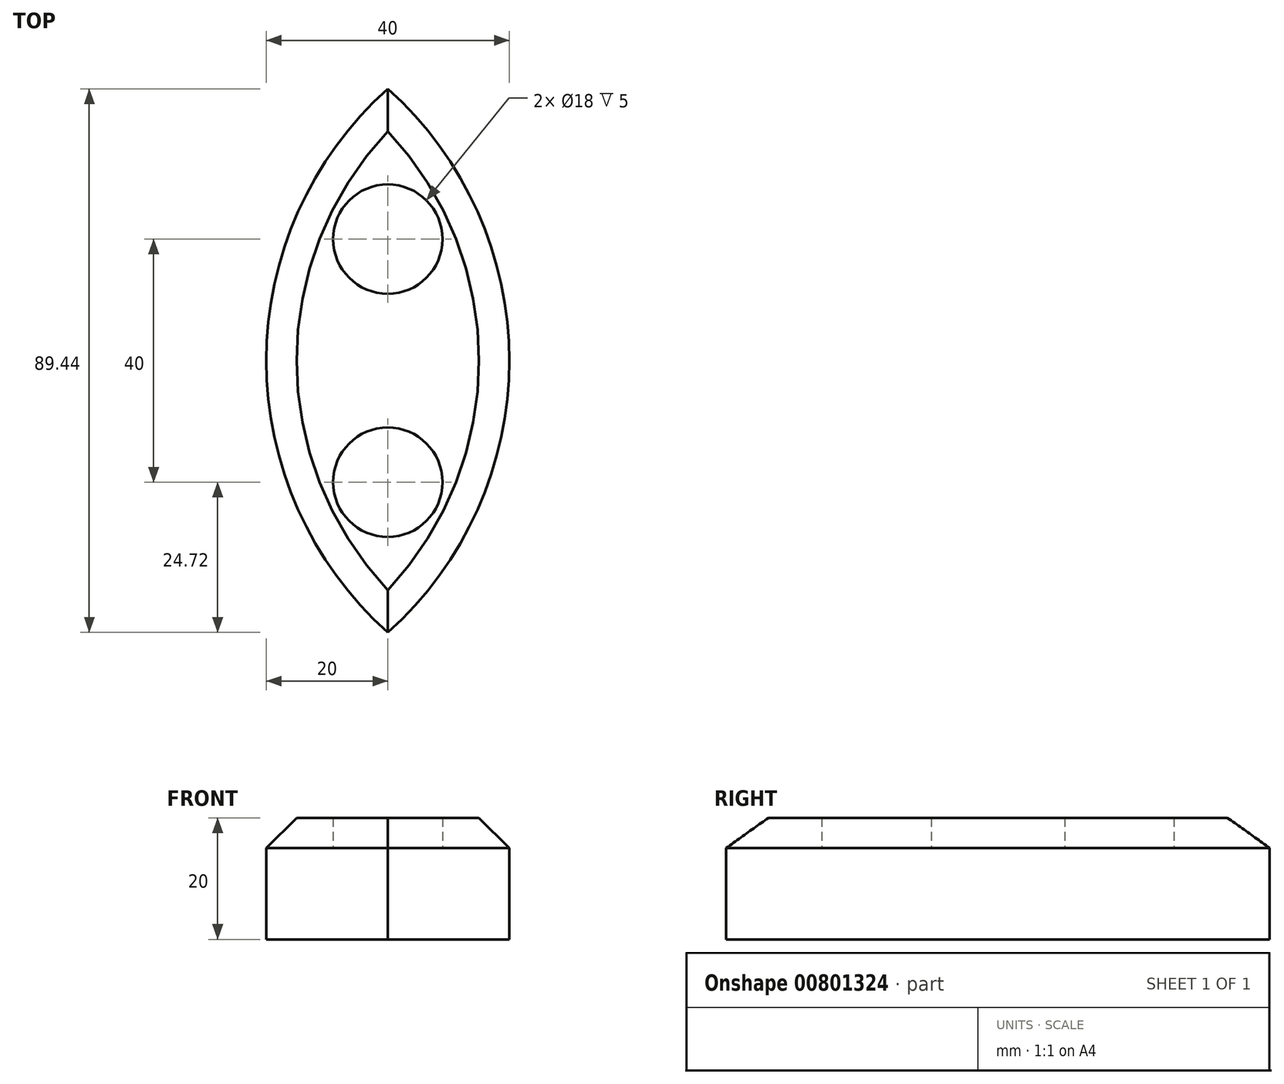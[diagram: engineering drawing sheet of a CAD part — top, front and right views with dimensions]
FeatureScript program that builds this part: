
annotation { "Feature Type Name" : "Feature", "Feature Type Description" : "" }
export const myFeature = defineFeature(function(context is Context, id is Id, definition is map)
    precondition{}
    {
        {
            var Q0;
            Q0=qCreatedBy(makeId("Top.planeOp"),FACE);
            var sketch = newSketch(context, id + "F0", { "sketchPlane" : qUnion([Q0])});
            skLineSegment(sketch, "E0", {"start": v(0, 0) * mm, "end": v(40, 0) * mm});
            skLineSegment(sketch, "E1", {"start": v(0, 0) * mm, "end": v(-40, 0) * mm});
            skPoint(sketch, "E2", {"position": v(-20, 0) * mm});
            skPoint(sketch, "E3", {"position": v(20, 0) * mm});
            skArc(sketch, "E4", {"start": v(0, -44.72) * mm, "mid": v(20, 0) * mm, "end": v(0, 44.72) * mm});
            skArc(sketch, "E5", {"start": v(0, 44.72) * mm, "mid": v(-20, 0) * mm, "end": v(0, -44.72) * mm});
            skPoint(sketch, "E6", {"position": v(0, 20) * mm});
            skPoint(sketch, "E7", {"position": v(0, -20) * mm});
            skCircle(sketch, "E8", {"center": v(0, 20) * mm, "radius": 9 * mm});
            skCircle(sketch, "E9", {"center": v(0, -20) * mm, "radius": 9 * mm});
            skSolve(sketch);
        }
        {
            var Q0;
            Q0=makeQuery(id+"F0.imprint","IMPRINT",FACE,{"disambiguationData":[TD([[makeQuery(id+"F0.imprint","IMPRINT",EDGE,{"derivedFrom":sQuery(id+"F0.wireOp",EDGE,"E8")}),-1.0]])]});
            var Q1;
            Q1=makeQuery(id+"F0.imprint","IMPRINT",FACE,{"disambiguationData":[TD([[makeQuery(id+"F0.imprint","IMPRINT",EDGE,{"derivedFrom":sQuery(id+"F0.wireOp",EDGE,"E9")}),-1.0]])]});
            extrude(context, id + "F1", {"entities" : qUnion([Q0, Q1]), "depth" : 20 * mm, "offsetDistance" : 25 * mm});
        }
        {
            var Q0;
            Q0=makeQuery(id+"F0.imprint","IMPRINT",FACE,{"disambiguationData":[TD([[makeQuery(id+"F0.imprint","IMPRINT",EDGE,{"derivedFrom":sQuery(id+"F0.wireOp",EDGE,"E9")}),1.0]])]});
            var Q1;
            Q1=makeQuery(id+"F0.imprint","IMPRINT",FACE,{"disambiguationData":[TD([[makeQuery(id+"F0.imprint","IMPRINT",EDGE,{"derivedFrom":sQuery(id+"F0.wireOp",EDGE,"E8")}),1.0]])]});
            extrude(context, id + "F2", {"entities" : qUnion([Q0, Q1]), "operationType" : NewBodyOperationType.ADD, "depth" : 15 * mm, "offsetDistance" : 25 * mm});
        }
        {
            var Q0;
            Q0=makeQuery(id+"F1.opExtrude","CAP_EDGE",EDGE,{"disambiguationData":[OSD([sQuery(id+"F0.wireOp",EDGE,"E4")])],"isStart":false});
            var Q1;
            Q1=makeQuery(id+"F1.opExtrude","CAP_EDGE",EDGE,{"disambiguationData":[OSD([sQuery(id+"F0.wireOp",EDGE,"E5")])],"isStart":false});
            chamfer(context, id + "F3", {"entities" : qUnion([Q0, Q1]), "chamferType" : ChamferType.TWO_OFFSETS, "width1" : 5 * mm, "oppositeDirection" : true, "width2" : 5 * mm, "tangentPropagation" : true});
        }
    });
